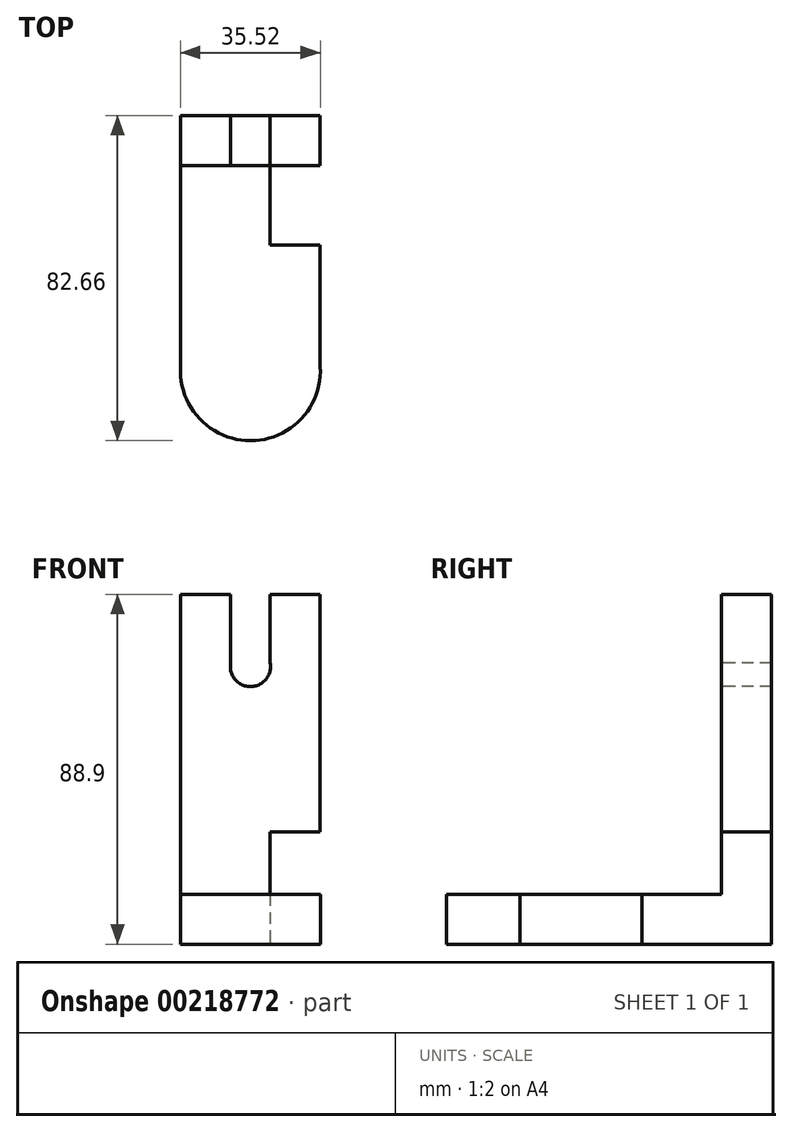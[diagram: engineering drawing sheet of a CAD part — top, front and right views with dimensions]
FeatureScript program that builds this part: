
annotation { "Feature Type Name" : "Feature", "Feature Type Description" : "" }
export const myFeature = defineFeature(function(context is Context, id is Id, definition is map)
    precondition{}
    {
        {
            var Q0;
            Q0=qCreatedBy(makeId("Top.planeOp"),FACE);
            var sketch = newSketch(context, id + "F0", { "sketchPlane" : qUnion([Q0])});
            skLineSegment(sketch, "E0.bottom", {"start": v(-17.73, -32.95) * mm, "end": v(17.73, -32.95) * mm});
            skLineSegment(sketch, "E0.top", {"start": v(-17.73, 32.95) * mm, "end": v(17.73, 32.95) * mm});
            skLineSegment(sketch, "E0.left", {"start": v(-17.73, -32.95) * mm, "end": v(-17.73, 32.95) * mm});
            skLineSegment(sketch, "E0.right", {"start": v(17.73, -32.95) * mm, "end": v(17.73, 32.95) * mm});
            skPoint(sketch, "E0.middle", {"position": v(0, 0) * mm});
            skCircle(sketch, "E1", {"center": v(0, -31.95) * mm, "radius": 17.76 * mm});
            skPoint(sketch, "E1.third.point", {"position": v(8.77, -47.39) * mm});
            skSolve(sketch);
        }
        {
            var Q0;
            Q0 = qSketchRegion(id + "F0", true);
            extrude(context, id + "F1", {"entities" : qUnion([Q0]), "depth" : 12.7 * mm});
        }
        {
            var Q0;
            Q0=makeQuery(id+"F1.opExtrude","CAP_FACE",FACE,{"disambiguationData":[OSD([sQuery(id+"F0.wireOp",EDGE,"E0.top"),sQuery(id+"F0.wireOp",EDGE,"E0.left"),sQuery(id+"F0.wireOp",EDGE,"E0.right"),sQuery(id+"F0.wireOp",EDGE,"E1")])],"isStart":false});
            var sketch = newSketch(context, id + "F2", { "sketchPlane" : qUnion([Q0])});
            skLineSegment(sketch, "E2", {"start": v(-17.73, 32.95) * mm, "end": v(-17.73, 20.21) * mm});
            skLineSegment(sketch, "E3", {"start": v(-17.73, 20.21) * mm, "end": v(17.73, 20.21) * mm});
            skLineSegment(sketch, "E4", {"start": v(17.73, 20.21) * mm, "end": v(17.73, 32.95) * mm});
            skLineSegment(sketch, "E5", {"start": v(17.73, 32.95) * mm, "end": v(-17.73, 32.95) * mm});
            skSolve(sketch);
        }
        {
            var Q0;
            Q0 = qSketchRegion(id + "F2", true);
            extrude(context, id + "F3", {"entities" : qUnion([Q0]), "operationType" : NewBodyOperationType.ADD, "depth" : 76.2 * mm});
        }
        {
            var Q0;
            Q0=makeQuery(id+"F3.opExtrude","SWEPT_FACE",FACE,{"disambiguationData":[OSD([sQuery(id+"F2.wireOp",EDGE,"E3")])]});
            var sketch = newSketch(context, id + "F4", { "sketchPlane" : qUnion([Q0])});
            skLineSegment(sketch, "E6", {"start": v(-5.03, 88.9) * mm, "end": v(-5.03, 71.39) * mm});
            skLineSegment(sketch, "E7", {"start": v(-5.03, 71.39) * mm, "end": v(5.03, 71.39) * mm});
            skLineSegment(sketch, "E8", {"start": v(5.03, 71.39) * mm, "end": v(5.03, 88.9) * mm});
            skLineSegment(sketch, "E9", {"start": v(5.03, 88.9) * mm, "end": v(-5.03, 88.9) * mm});
            skCircle(sketch, "E10", {"center": v(0, 70.55) * mm, "radius": 5.1 * mm});
            skPoint(sketch, "E10.third.point", {"position": v(5.03, 69.7) * mm});
            skSolve(sketch);
        }
        {
            var Q0;
            Q0 = qSketchRegion(id + "F4", true);
            extrude(context, id + "F5", {"entities" : qUnion([Q0]), "operationType" : NewBodyOperationType.REMOVE, "oppositeDirection" : true, "depth" : 25.4 * mm});
        }
        {
            var Q0;
            Q0=makeQuery(id+"F3.boolean.opBoolean","MERGE",FACE,{"derivedFrom":[makeQuery(id+"F1.opExtrude","SWEPT_FACE",FACE,{"disambiguationData":[OSD([sQuery(id+"F0.wireOp",EDGE,"E0.right")])]}),makeQuery(id+"F3.opExtrude","SWEPT_FACE",FACE,{"disambiguationData":[OSD([sQuery(id+"F2.wireOp",EDGE,"E4")])]})]});
            var sketch = newSketch(context, id + "F6", { "sketchPlane" : qUnion([Q0])});
            skLineSegment(sketch, "E11", {"start": v(32.95, 0) * mm, "end": v(32.95, 28.49) * mm});
            skLineSegment(sketch, "E12", {"start": v(32.95, 28.49) * mm, "end": v(20.21, 28.49) * mm});
            skLineSegment(sketch, "E13", {"start": v(20.21, 28.49) * mm, "end": v(20.21, 12.7) * mm});
            skLineSegment(sketch, "E14", {"start": v(20.21, 12.7) * mm, "end": v(0, 12.7) * mm});
            skLineSegment(sketch, "E15", {"start": v(0, 12.7) * mm, "end": v(0, 0) * mm});
            skSolve(sketch);
        }
        {
            var Q0;
            {var subQ1=sQuery(id+"F6.wireOp",EDGE,"E11");Q0=makeQuery(id+"F6.imprint","IMPRINT",FACE,{"disambiguationData":[TD([[makeQuery(id+"F6.imprint","IMPRINT",EDGE,{"derivedFrom":subQ1}),-1.0]])]});}
            extrude(context, id + "F7", {"entities" : qUnion([Q0]), "operationType" : NewBodyOperationType.REMOVE, "oppositeDirection" : true, "depth" : 12.7 * mm});
        }
    });
